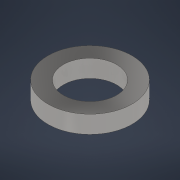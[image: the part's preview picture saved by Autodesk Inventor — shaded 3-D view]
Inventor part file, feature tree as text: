
AUTODESK INVENTOR PART (.ipt)
format: ipt  version: 2021 (Build 250183000, 183)  size: 217,600 bytes
history: native  units: mm
features: extrude x1, sketch x1
ambient origin geometry x8: Origin, YZ Plane, XZ Plane, XY Plane, X Axis, Y Axis, Z Axis, Center Point
bodies: Volumenkörper1 (feature_tree)
feature tree (2):
  extrude  "Extrusion1"  Depth=5.0mm TaperAngle=0.0deg
  sketch  "Skizze1"  dims[d0=24.0mm d2=5.0mm d3=0.0mm d5=15.2mm]
